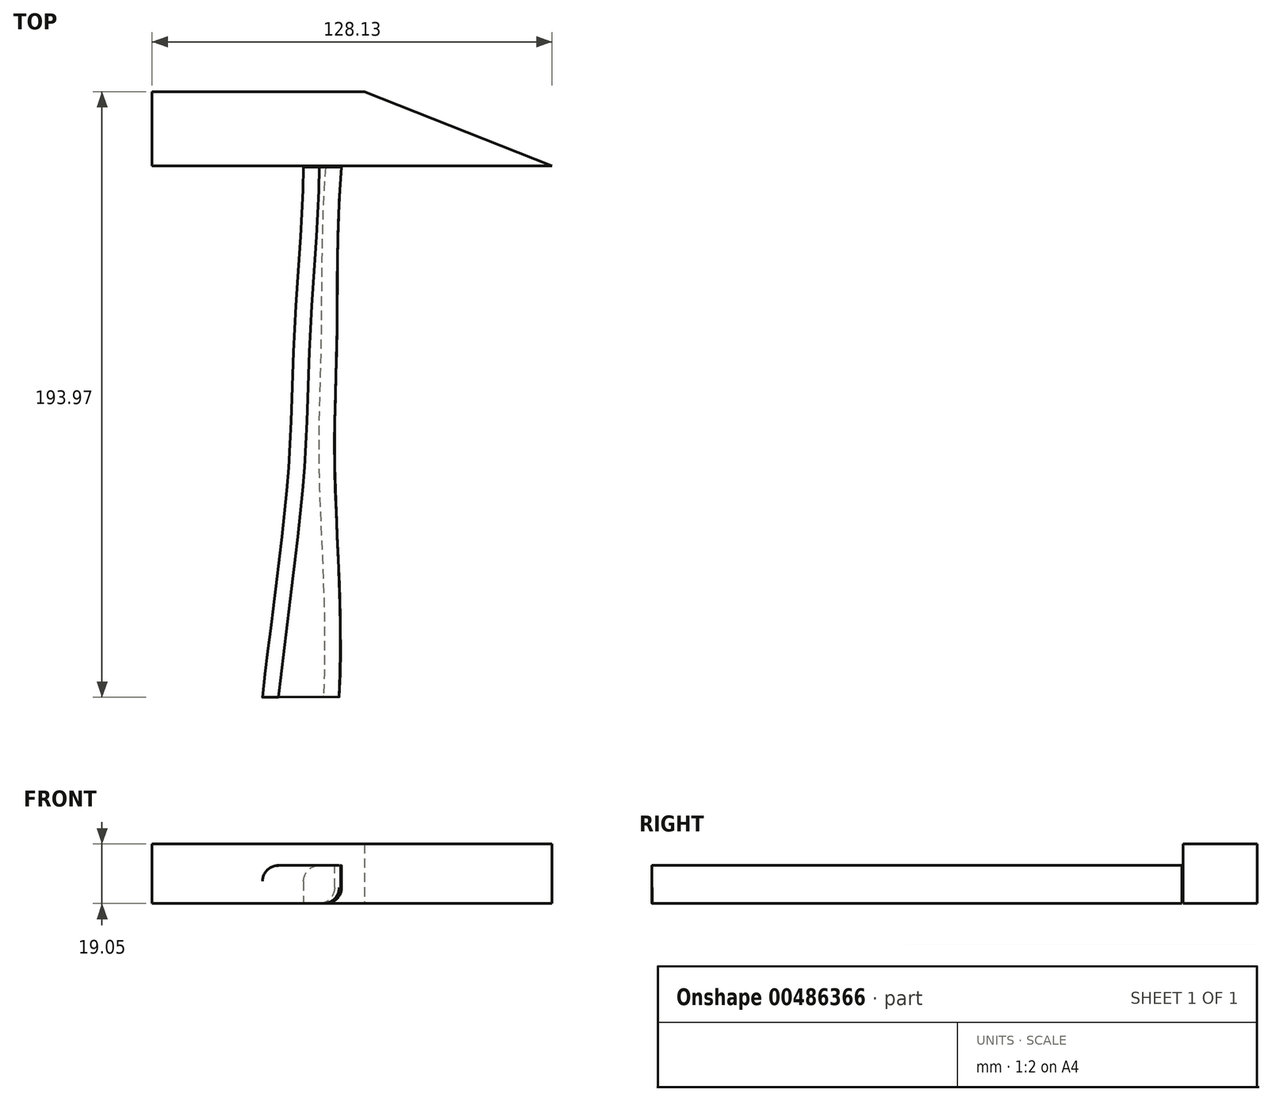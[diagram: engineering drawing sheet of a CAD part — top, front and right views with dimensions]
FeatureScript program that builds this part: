
annotation { "Feature Type Name" : "Feature", "Feature Type Description" : "" }
export const myFeature = defineFeature(function(context is Context, id is Id, definition is map)
    precondition{}
    {
        {
            var Q0;
            Q0=qCreatedBy(makeId("Top.planeOp"),FACE);
            var sketch = newSketch(context, id + "F0", { "sketchPlane" : qUnion([Q0])});
            skLineSegment(sketch, "E0", {"start": v(-57.93, 33.98) * mm, "end": v(-9.08, 33.98) * mm});
            skLineSegment(sketch, "E1", {"start": v(18.95, 10.2) * mm, "end": v(-57.93, 10.2) * mm});
            skLineSegment(sketch, "E2", {"start": v(18.95, 10.2) * mm, "end": v(31.32, 10.2) * mm});
            skLineSegment(sketch, "E3", {"start": v(31.32, 10.2) * mm, "end": v(39.14, 10.2) * mm});
            skLineSegment(sketch, "E4", {"start": v(-57.93, 10.2) * mm, "end": v(-77.17, 10.2) * mm});
            skLineSegment(sketch, "E5", {"start": v(-57.93, 33.98) * mm, "end": v(-77.17, 33.98) * mm});
            skLineSegment(sketch, "E6", {"start": v(-77.17, 10.2) * mm, "end": v(-77.17, 33.98) * mm});
            skLineSegment(sketch, "E7", {"start": v(39.14, 10.2) * mm, "end": v(50.96, 10.2) * mm});
            skLineSegment(sketch, "E8", {"start": v(-9.08, 33.98) * mm, "end": v(50.96, 10.2) * mm});
            skSolve(sketch);
        }
        {
            var Q0;
            Q0 = qSketchRegion(id + "F0", true);
            extrude(context, id + "F1", {"entities" : qUnion([Q0]), "depth" : 19.05 * mm});
        }
        {
            var Q0;
            Q0=qCreatedBy(makeId("Top.planeOp"),FACE);
            var sketch = newSketch(context, id + "F2", { "sketchPlane" : qUnion([Q0])});
            skPoint(sketch, "E9.1.internal.orphan", {"position": v(-56.64, 0) * mm});
            skPoint(sketch, "E10.2.internal.orphan", {"position": v(0, -88.66) * mm});
            skFitSpline(sketch, "E11", {"points": [v(-16.5, 9.8) * mm, v(-17.97, -45.14) * mm, v(-18.62, -88.66) * mm, v(-17.22, -159.86) * mm], "startDerivative": vector(-14.41, -171.5) * mm, "endDerivative": vector(-10.4, -208.93) * mm});
            skFitSpline(sketch, "E12", {"points": [v(-28.67, 9.83) * mm, v(-31.72, -45.47) * mm, v(-33.66, -89.14) * mm, v(-41.83, -159.99) * mm], "startDerivative": vector(-3.74, -179.78) * mm, "endDerivative": vector(-22.66, -201.72) * mm});
            skLineSegment(sketch, "E13", {"start": v(-41.83, -159.99) * mm, "end": v(-17.22, -159.86) * mm});
            skLineSegment(sketch, "E14", {"start": v(-28.67, 9.83) * mm, "end": v(-16.5, 9.8) * mm});
            skSolve(sketch);
        }
        {
            var Q0;
            Q0 = qSketchRegion(id + "F2", true);
            extrude(context, id + "F3", {"entities" : qUnion([Q0]), "depth" : 12.2 * mm});
        }
        {
            var Q0;
            Q0=makeQuery(id+"F3.opExtrude","CAP_EDGE",EDGE,{"disambiguationData":[OSD([sQuery(id+"F2.wireOp",EDGE,"E12")])],"isStart":false});
            fillet(context, id + "F4", {"entities" : qUnion([Q0]), "radius" : 5.08 * mm, "tangentPropagation" : true, "allowEdgeOverflow" : false});
        }
        {
            var Q0;
            Q0=makeQuery(id+"F3.opExtrude","CAP_EDGE",EDGE,{"disambiguationData":[OSD([sQuery(id+"F2.wireOp",EDGE,"E11")])],"isStart":false});
            var Q1;
            Q1=makeQuery(id+"F3.opExtrude","CAP_EDGE",EDGE,{"disambiguationData":[OSD([sQuery(id+"F2.wireOp",EDGE,"E13")])],"isStart":false});
            var Q2;
            Q2=makeQuery(id+"F3.opExtrude","CAP_EDGE",EDGE,{"disambiguationData":[OSD([sQuery(id+"F2.wireOp",EDGE,"E12")])],"isStart":true});
            var Q3;
            Q3=makeQuery(id+"F3.opExtrude","CAP_EDGE",EDGE,{"disambiguationData":[OSD([sQuery(id+"F2.wireOp",EDGE,"E13")])],"isStart":true});
            var Q4;
            Q4=makeQuery(id+"F4.opFillet","BLEND_EDGE",EDGE,{"blendedFrom":[makeQuery(id+"F3.opExtrude","CAP_EDGE",EDGE,{"disambiguationData":[OSD([sQuery(id+"F2.wireOp",EDGE,"E12")])],"isStart":false}),makeQuery(id+"F3.opExtrude","SWEPT_FACE",FACE,{"disambiguationData":[OSD([sQuery(id+"F2.wireOp",EDGE,"E13")])]})],"blendedInto":[makeQuery(id+"F3.opExtrude","SWEPT_FACE",FACE,{"disambiguationData":[OSD([sQuery(id+"F2.wireOp",EDGE,"E13")])]})]});
            var Q5;
            Q5=makeQuery(id+"F3.opExtrude","SWEPT_FACE",FACE,{"disambiguationData":[OSD([sQuery(id+"F2.wireOp",EDGE,"E13")])]});
            fillet(context, id + "F5", {"entities" : qUnion([Q0, Q1, Q2, Q3, Q4, Q5]), "radius" : 0.03 * mm, "tangentPropagation" : true, "allowEdgeOverflow" : false});
        }
        {
            var Q0;
            Q0=makeQuery(id+"F3.opExtrude","CAP_EDGE",EDGE,{"disambiguationData":[OSD([sQuery(id+"F2.wireOp",EDGE,"E11")])],"isStart":false});
            var Q1;
            Q1=makeQuery(id+"F3.opExtrude","CAP_EDGE",EDGE,{"disambiguationData":[OSD([sQuery(id+"F2.wireOp",EDGE,"E11")])],"isStart":true});
            var Q2;
            Q2=makeQuery(id+"F3.opExtrude","CAP_EDGE",EDGE,{"disambiguationData":[OSD([sQuery(id+"F2.wireOp",EDGE,"E12")])],"isStart":true});
            fillet(context, id + "F6", {"entities" : qUnion([Q0, Q1, Q2]), "radius" : 5.08 * mm, "tangentPropagation" : true, "allowEdgeOverflow" : false});
        }
    });
